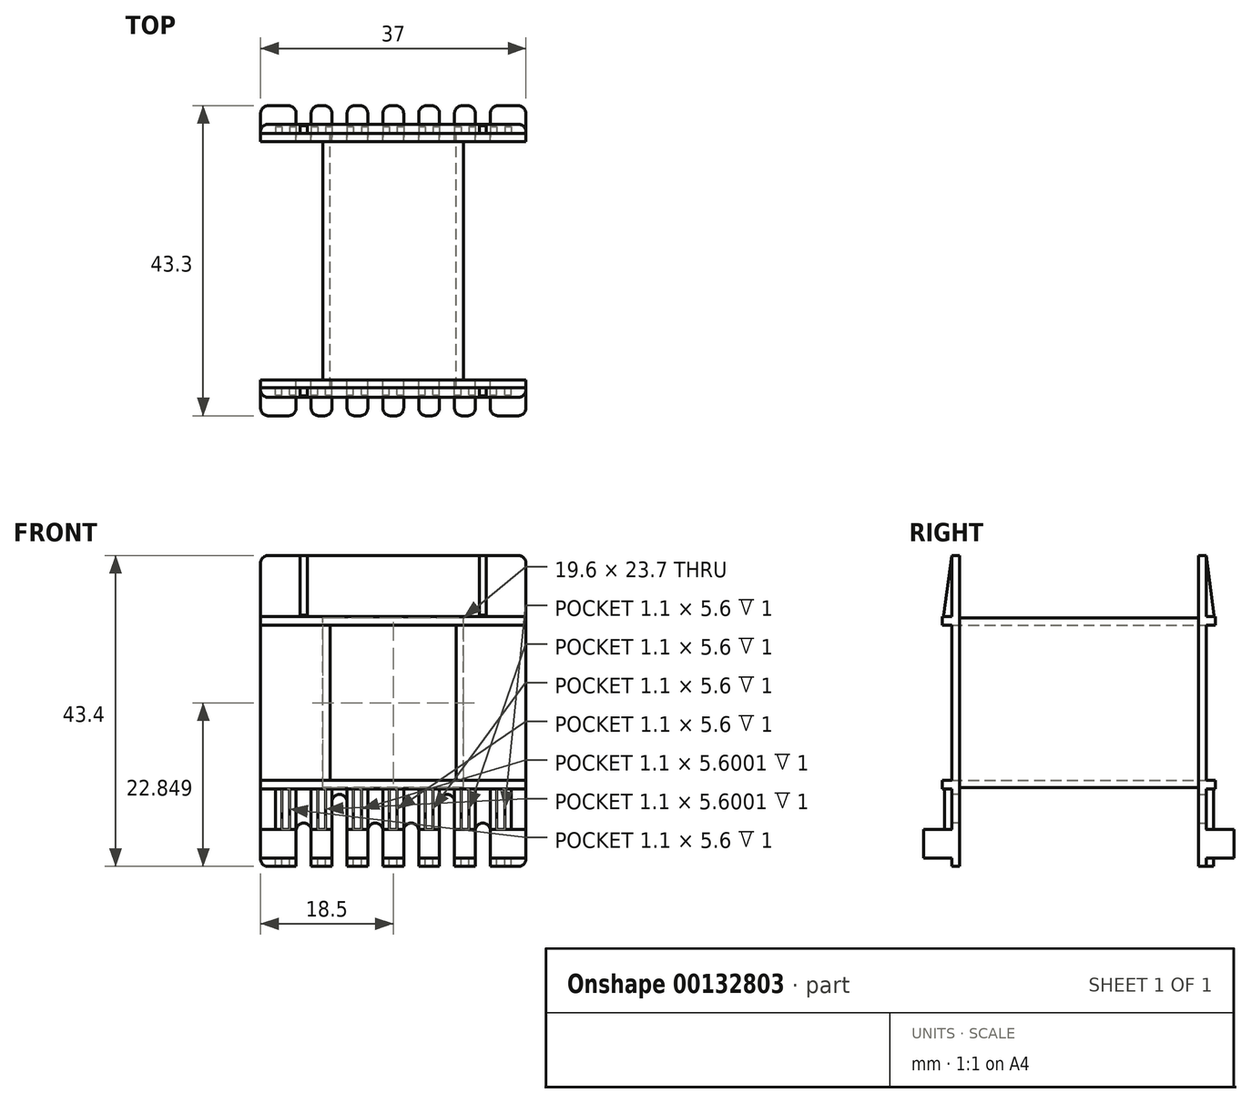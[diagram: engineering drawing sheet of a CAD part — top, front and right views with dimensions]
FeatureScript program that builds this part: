
annotation { "Feature Type Name" : "Feature", "Feature Type Description" : "" }
export const myFeature = defineFeature(function(context is Context, id is Id, definition is map)
    precondition{}
    {
        {
            var Q0;
            Q0=qCreatedBy(makeId("Front.planeOp"),FACE);
            var sketch = newSketch(context, id + "F0", { "sketchPlane" : qUnion([Q0])});
            skLineSegment(sketch, "E0.bottom", {"start": v(-18.5, -0.08) * mm, "end": v(18.5, -0.08) * mm});
            skLineSegment(sketch, "E0.top", {"start": v(-18.5, 43.32) * mm, "end": v(18.5, 43.32) * mm});
            skLineSegment(sketch, "E0.left", {"start": v(-18.5, -0.08) * mm, "end": v(-18.5, 43.32) * mm});
            skLineSegment(sketch, "E0.right", {"start": v(18.5, -0.08) * mm, "end": v(18.5, 43.32) * mm});
            skSolve(sketch);
        }
        {
            var Q0;
            Q0=makeQuery(id+"F0.imprint","IMPRINT",FACE,{"disambiguationData":[TD([[makeQuery(id+"F0.imprint","IMPRINT",EDGE,{"derivedFrom":sQuery(id+"F0.wireOp",EDGE,"E0.bottom")}),1.0]])]});
            var sketch = newSketch(context, id + "F1", { "sketchPlane" : qUnion([Q0])});
            skLineSegment(sketch, "E1.bottom", {"start": v(-8.8, 11.92) * mm, "end": v(8.8, 11.92) * mm});
            skLineSegment(sketch, "E1.top", {"start": v(-8.8, 33.62) * mm, "end": v(8.8, 33.62) * mm});
            skLineSegment(sketch, "E1.left", {"start": v(-8.8, 11.92) * mm, "end": v(-8.8, 33.62) * mm});
            skLineSegment(sketch, "E1.right", {"start": v(8.8, 11.92) * mm, "end": v(8.8, 33.62) * mm});
            skSolve(sketch);
        }
        {
            var Q0;
            Q0=makeQuery(id+"F1.imprint","IMPRINT",FACE,{"disambiguationData":[TD([[makeQuery(id+"F1.imprint","IMPRINT",EDGE,{"derivedFrom":sQuery(id+"F1.wireOp",EDGE,"E1.bottom")}),-1.0]])]});
            extrude(context, id + "F2", {"entities" : qUnion([Q0]), "depth" : 17.75 * mm, "hasSecondDirection" : true, "secondDirectionOppositeDirection" : false, "secondDirectionDepth" : 16.65 * mm});
        }
        {
            var Q0;
            Q0=makeQuery(id+"F2.opExtrude","CAP_FACE",FACE,{"disambiguationData":[OSD([sQuery(id+"F0.wireOp",EDGE,"E0.bottom"),sQuery(id+"F0.wireOp",EDGE,"E0.top"),sQuery(id+"F0.wireOp",EDGE,"E0.left"),sQuery(id+"F0.wireOp",EDGE,"E0.right"),sQuery(id+"F1.wireOp",EDGE,"E1.bottom"),sQuery(id+"F1.wireOp",EDGE,"E1.top"),sQuery(id+"F1.wireOp",EDGE,"E1.left"),sQuery(id+"F1.wireOp",EDGE,"E1.right")])],"isStart":false});
            var sketch = newSketch(context, id + "F3", { "sketchPlane" : qUnion([Q0])});
            skLineSegment(sketch, "E2.bottom", {"start": v(-18.5, 33.62) * mm, "end": v(18.5, 33.62) * mm});
            skLineSegment(sketch, "E2.top", {"start": v(-18.5, 34.82) * mm, "end": v(18.5, 34.82) * mm});
            skLineSegment(sketch, "E2.left", {"start": v(-18.5, 33.62) * mm, "end": v(-18.5, 34.82) * mm});
            skLineSegment(sketch, "E2.right", {"start": v(18.5, 33.62) * mm, "end": v(18.5, 34.82) * mm});
            skSolve(sketch);
        }
        {
            var Q0;
            Q0=qSketchRegion(id+"F3",true);
            extrude(context, id + "F4", {"entities" : qUnion([Q0]), "operationType" : NewBodyOperationType.ADD, "depth" : 1.3 * mm});
        }
        {
            var Q0;
            {var subQ0=sQuery(id+"F1.wireOp",EDGE,"E1.left");var subQ1=sQuery(id+"F1.wireOp",EDGE,"E1.top");var subQ2=sQuery(id+"F0.wireOp",EDGE,"E0.right");var subQ3=sQuery(id+"F1.wireOp",EDGE,"E1.right");var subQ4=sQuery(id+"F1.wireOp",EDGE,"E1.bottom");var subQ5=sQuery(id+"F0.wireOp",EDGE,"E0.bottom");var subQ6=sQuery(id+"F0.wireOp",EDGE,"E0.left");Q0=makeQuery(id+"F4.boolean.opBoolean","SPLIT",FACE,{"disambiguationData":[TD([makeQuery(id+"F2.opExtrude","SWEPT_FACE",FACE,{"disambiguationData":[OSD([subQ4])]})])],"derivedFrom":makeQuery(id+"F2.opExtrude","CAP_FACE",FACE,{"disambiguationData":[OSD([subQ5,sQuery(id+"F0.wireOp",EDGE,"E0.top"),subQ6,subQ2,subQ4,subQ1,subQ0,subQ3])],"isStart":false})});}
            var sketch = newSketch(context, id + "F5", { "sketchPlane" : qUnion([Q0])});
            skLineSegment(sketch, "E3.bottom", {"start": v(-18.5, 10.72) * mm, "end": v(18.5, 10.72) * mm});
            skLineSegment(sketch, "E3.top", {"start": v(-18.5, 11.92) * mm, "end": v(18.5, 11.92) * mm});
            skLineSegment(sketch, "E3.left", {"start": v(-18.5, 10.72) * mm, "end": v(-18.5, 11.92) * mm});
            skLineSegment(sketch, "E3.right", {"start": v(18.5, 10.72) * mm, "end": v(18.5, 11.92) * mm});
            skSolve(sketch);
        }
        {
            var Q0;
            Q0=makeQuery(id+"F5.imprint","IMPRINT",FACE,{"disambiguationData":[TD([[makeQuery(id+"F5.imprint","IMPRINT",EDGE,{"derivedFrom":sQuery(id+"F5.wireOp",EDGE,"E3.bottom")}),1.0]])]});
            extrude(context, id + "F6", {"entities" : qUnion([Q0]), "operationType" : NewBodyOperationType.ADD, "depth" : 1.3 * mm});
        }
        {
            var Q0;
            {var subQ0=sQuery(id+"F0.wireOp",EDGE,"E0.right");var subQ1=sQuery(id+"F0.wireOp",EDGE,"E0.left");var subQ2=sQuery(id+"F0.wireOp",EDGE,"E0.top");Q0=makeQuery(id+"F4.boolean.opBoolean","SPLIT",FACE,{"disambiguationData":[TD([makeQuery(id+"F2.opExtrude","SWEPT_FACE",FACE,{"disambiguationData":[OSD([subQ2])]})])],"derivedFrom":makeQuery(id+"F2.opExtrude","CAP_FACE",FACE,{"disambiguationData":[OSD([sQuery(id+"F0.wireOp",EDGE,"E0.bottom"),subQ2,subQ1,subQ0,sQuery(id+"F1.wireOp",EDGE,"E1.bottom"),sQuery(id+"F1.wireOp",EDGE,"E1.top"),sQuery(id+"F1.wireOp",EDGE,"E1.left"),sQuery(id+"F1.wireOp",EDGE,"E1.right")])],"isStart":false})});}
            var sketch = newSketch(context, id + "F7", { "sketchPlane" : qUnion([Q0])});
            skLineSegment(sketch, "E4.bottom", {"start": v(-13, 34.82) * mm, "end": v(-12, 34.82) * mm});
            skLineSegment(sketch, "E4.top", {"start": v(-13, 43.32) * mm, "end": v(-12, 43.32) * mm});
            skLineSegment(sketch, "E4.left", {"start": v(-13, 34.82) * mm, "end": v(-13, 43.32) * mm});
            skLineSegment(sketch, "E4.right", {"start": v(-12, 34.82) * mm, "end": v(-12, 43.32) * mm});
            skSolve(sketch);
        }
        {
            var Q0;
            {var subQ1=sQuery(id+"F0.wireOp",EDGE,"E0.top");var subQ2=makeQuery(id+"F2.opExtrude","SWEPT_FACE",FACE,{"disambiguationData":[OSD([subQ1])]});var subQ4=sQuery(id+"F0.wireOp",EDGE,"E0.right");var subQ5=makeQuery(id+"F2.opExtrude","SWEPT_FACE",FACE,{"disambiguationData":[OSD([subQ4])]});var subQ6=sQuery(id+"F0.wireOp",EDGE,"E0.left");Q0=makeQuery(id+"Fz3WZ2JE0xqVuv4_1.boolean.opBoolean","SPLIT",FACE,{"disambiguationData":[TD([subQ5])],"derivedFrom":makeQuery(id+"F4.boolean.opBoolean","SPLIT",FACE,{"disambiguationData":[TD([subQ2])],"derivedFrom":makeQuery(id+"F2.opExtrude","CAP_FACE",FACE,{"disambiguationData":[OSD([sQuery(id+"F0.wireOp",EDGE,"E0.bottom"),subQ1,subQ6,subQ4,sQuery(id+"F1.wireOp",EDGE,"E1.bottom"),sQuery(id+"F1.wireOp",EDGE,"E1.top"),sQuery(id+"F1.wireOp",EDGE,"E1.left"),sQuery(id+"F1.wireOp",EDGE,"E1.right")])],"isStart":false})})});}
            var sketch = newSketch(context, id + "F8", { "sketchPlane" : qUnion([Q0])});
            skLineSegment(sketch, "E5.bottom", {"start": v(12, 34.82) * mm, "end": v(13, 34.82) * mm});
            skLineSegment(sketch, "E5.top", {"start": v(12, 43.32) * mm, "end": v(13, 43.32) * mm});
            skLineSegment(sketch, "E5.left", {"start": v(12, 34.82) * mm, "end": v(12, 43.32) * mm});
            skLineSegment(sketch, "E5.right", {"start": v(13, 34.82) * mm, "end": v(13, 43.32) * mm});
            skSolve(sketch);
        }
        {
            var Q0;
            Q0=makeQuery(id+"F7.imprint","IMPRINT",FACE,{"disambiguationData":[TD([[makeQuery(id+"F7.imprint","IMPRINT",EDGE,{"derivedFrom":sQuery(id+"F7.wireOp",EDGE,"E4.bottom")}),1.0]])]});
            extrude(context, id + "F9", {"entities" : qUnion([Q0]), "operationType" : NewBodyOperationType.ADD, "depth" : 1.1 * mm});
        }
        {
            var Q0;
            Q0=makeQuery(id+"F8.imprint","IMPRINT",FACE,{"disambiguationData":[TD([[makeQuery(id+"F8.imprint","IMPRINT",EDGE,{"derivedFrom":sQuery(id+"F8.wireOp",EDGE,"E5.bottom")}),1.0]])]});
            extrude(context, id + "F10", {"entities" : qUnion([Q0]), "operationType" : NewBodyOperationType.ADD, "depth" : 1.1 * mm});
        }
        {
            var Q0;
            Q0=makeQuery(id+"F9.opExtrude","CAP_EDGE",EDGE,{"disambiguationData":[OSD([sQuery(id+"F7.wireOp",EDGE,"E4.top")])],"isStart":false});
            var Q1;
            Q1=makeQuery(id+"F10.opExtrude","CAP_EDGE",EDGE,{"disambiguationData":[OSD([sQuery(id+"F8.wireOp",EDGE,"E5.top")])],"isStart":false});
            chamfer(context, id + "F11", {"entities" : qUnion([Q0, Q1]), "chamferType" : ChamferType.TWO_OFFSETS, "width1" : 1.1 * mm, "oppositeDirection" : false, "width2" : 8.3 * mm, "tangentPropagation" : true});
        }
        {
            var Q0;
            {var subQ1=sQuery(id+"F0.wireOp",EDGE,"E0.right");var subQ3=sQuery(id+"F0.wireOp",EDGE,"E0.left");var subQ5=sQuery(id+"F0.wireOp",EDGE,"E0.bottom");var subQ6=makeQuery(id+"F2.opExtrude","SWEPT_FACE",FACE,{"disambiguationData":[OSD([subQ5])]});var subQ8=sQuery(id+"F1.wireOp",EDGE,"E1.left");var subQ9=sQuery(id+"F1.wireOp",EDGE,"E1.top");var subQ10=sQuery(id+"F1.wireOp",EDGE,"E1.right");var subQ11=sQuery(id+"F1.wireOp",EDGE,"E1.bottom");Q0=makeQuery(id+"F6.boolean.opBoolean","SPLIT",FACE,{"disambiguationData":[TD([subQ6])],"derivedFrom":makeQuery(id+"F4.boolean.opBoolean","SPLIT",FACE,{"disambiguationData":[TD([makeQuery(id+"F2.opExtrude","SWEPT_FACE",FACE,{"disambiguationData":[OSD([subQ11])]})])],"derivedFrom":makeQuery(id+"F2.opExtrude","CAP_FACE",FACE,{"disambiguationData":[OSD([subQ5,sQuery(id+"F0.wireOp",EDGE,"E0.top"),subQ3,subQ1,subQ11,subQ9,subQ8,subQ10])],"isStart":false})})});}
            var sketch = newSketch(context, id + "F12", { "sketchPlane" : qUnion([Q0])});
            skLineSegment(sketch, "E6.bottom", {"start": v(-16.45, -0.08) * mm, "end": v(-15.55, -0.08) * mm});
            skLineSegment(sketch, "E6.top", {"start": v(-16.45, 10.72) * mm, "end": v(-15.55, 10.72) * mm});
            skLineSegment(sketch, "E6.left", {"start": v(-16.45, -0.08) * mm, "end": v(-16.45, 10.72) * mm});
            skLineSegment(sketch, "E6.right", {"start": v(-15.55, -0.08) * mm, "end": v(-15.55, 10.72) * mm});
            skLineSegment(sketch, "E7.bottom", {"start": v(-14.45, -0.08) * mm, "end": v(-13.55, -0.08) * mm});
            skLineSegment(sketch, "E7.top", {"start": v(-14.45, 10.72) * mm, "end": v(-13.55, 10.72) * mm});
            skLineSegment(sketch, "E7.left", {"start": v(-14.45, -0.08) * mm, "end": v(-14.45, 10.72) * mm});
            skLineSegment(sketch, "E7.right", {"start": v(-13.55, -0.08) * mm, "end": v(-13.55, 10.72) * mm});
            skLineSegment(sketch, "E8.bottom", {"start": v(-11.45, -0.08) * mm, "end": v(-10.55, -0.08) * mm});
            skLineSegment(sketch, "E8.top", {"start": v(-11.45, 10.72) * mm, "end": v(-10.55, 10.72) * mm});
            skLineSegment(sketch, "E8.left", {"start": v(-11.45, -0.08) * mm, "end": v(-11.45, 10.72) * mm});
            skLineSegment(sketch, "E8.right", {"start": v(-10.55, -0.08) * mm, "end": v(-10.55, 10.72) * mm});
            skLineSegment(sketch, "E9.bottom", {"start": v(-9.45, -0.08) * mm, "end": v(-8.55, -0.08) * mm});
            skLineSegment(sketch, "E9.top", {"start": v(-9.45, 10.72) * mm, "end": v(-8.55, 10.72) * mm});
            skLineSegment(sketch, "E9.left", {"start": v(-9.45, -0.08) * mm, "end": v(-9.45, 10.72) * mm});
            skLineSegment(sketch, "E9.right", {"start": v(-8.55, -0.08) * mm, "end": v(-8.55, 10.72) * mm});
            skLineSegment(sketch, "E10.bottom", {"start": v(-6.45, -0.08) * mm, "end": v(-5.55, -0.08) * mm});
            skLineSegment(sketch, "E10.top", {"start": v(-6.45, 10.72) * mm, "end": v(-5.55, 10.72) * mm});
            skLineSegment(sketch, "E10.left", {"start": v(-6.45, -0.08) * mm, "end": v(-6.45, 10.72) * mm});
            skLineSegment(sketch, "E10.right", {"start": v(-5.55, -0.08) * mm, "end": v(-5.55, 10.72) * mm});
            skLineSegment(sketch, "E11.bottom", {"start": v(-1.45, -0.08) * mm, "end": v(-0.55, -0.08) * mm});
            skLineSegment(sketch, "E11.top", {"start": v(-1.45, 10.72) * mm, "end": v(-0.55, 10.72) * mm});
            skLineSegment(sketch, "E11.left", {"start": v(-1.45, -0.08) * mm, "end": v(-1.45, 10.72) * mm});
            skLineSegment(sketch, "E11.right", {"start": v(-0.55, -0.08) * mm, "end": v(-0.55, 10.72) * mm});
            skLineSegment(sketch, "E12.bottom", {"start": v(0.55, -0.08) * mm, "end": v(1.45, -0.08) * mm});
            skLineSegment(sketch, "E12.top", {"start": v(0.55, 10.72) * mm, "end": v(1.45, 10.72) * mm});
            skLineSegment(sketch, "E12.left", {"start": v(0.55, -0.08) * mm, "end": v(0.55, 10.72) * mm});
            skLineSegment(sketch, "E12.right", {"start": v(1.45, -0.08) * mm, "end": v(1.45, 10.72) * mm});
            skLineSegment(sketch, "E13.bottom", {"start": v(3.55, -0.08) * mm, "end": v(4.45, -0.08) * mm});
            skLineSegment(sketch, "E13.top", {"start": v(3.55, 10.72) * mm, "end": v(4.45, 10.72) * mm});
            skLineSegment(sketch, "E13.left", {"start": v(3.55, -0.08) * mm, "end": v(3.55, 10.72) * mm});
            skLineSegment(sketch, "E13.right", {"start": v(4.45, -0.08) * mm, "end": v(4.45, 10.72) * mm});
            skLineSegment(sketch, "E14.bottom", {"start": v(5.55, -0.08) * mm, "end": v(6.45, -0.08) * mm});
            skLineSegment(sketch, "E14.top", {"start": v(5.55, 10.72) * mm, "end": v(6.45, 10.72) * mm});
            skLineSegment(sketch, "E14.left", {"start": v(5.55, -0.08) * mm, "end": v(5.55, 10.72) * mm});
            skLineSegment(sketch, "E14.right", {"start": v(6.45, -0.08) * mm, "end": v(6.45, 10.72) * mm});
            skLineSegment(sketch, "E15.bottom", {"start": v(8.55, -0.08) * mm, "end": v(9.45, -0.08) * mm});
            skLineSegment(sketch, "E15.top", {"start": v(8.55, 10.72) * mm, "end": v(9.45, 10.72) * mm});
            skLineSegment(sketch, "E15.left", {"start": v(8.55, -0.08) * mm, "end": v(8.55, 10.72) * mm});
            skLineSegment(sketch, "E15.right", {"start": v(9.45, -0.08) * mm, "end": v(9.45, 10.72) * mm});
            skLineSegment(sketch, "E16.bottom", {"start": v(10.55, -0.08) * mm, "end": v(11.45, -0.08) * mm});
            skLineSegment(sketch, "E16.top", {"start": v(10.55, 10.72) * mm, "end": v(11.45, 10.72) * mm});
            skLineSegment(sketch, "E16.left", {"start": v(10.55, -0.08) * mm, "end": v(10.55, 10.72) * mm});
            skLineSegment(sketch, "E16.right", {"start": v(11.45, -0.08) * mm, "end": v(11.45, 10.72) * mm});
            skLineSegment(sketch, "E17.bottom", {"start": v(13.55, -0.08) * mm, "end": v(14.45, -0.08) * mm});
            skLineSegment(sketch, "E17.top", {"start": v(13.55, 10.72) * mm, "end": v(14.45, 10.72) * mm});
            skLineSegment(sketch, "E17.left", {"start": v(13.55, -0.08) * mm, "end": v(13.55, 10.72) * mm});
            skLineSegment(sketch, "E17.right", {"start": v(14.45, -0.08) * mm, "end": v(14.45, 10.72) * mm});
            skLineSegment(sketch, "E18.bottom", {"start": v(15.55, -0.08) * mm, "end": v(16.45, -0.08) * mm});
            skLineSegment(sketch, "E18.top", {"start": v(15.55, 10.72) * mm, "end": v(16.45, 10.72) * mm});
            skLineSegment(sketch, "E18.left", {"start": v(15.55, -0.08) * mm, "end": v(15.55, 10.72) * mm});
            skLineSegment(sketch, "E18.right", {"start": v(16.45, -0.08) * mm, "end": v(16.45, 10.72) * mm});
            skLineSegment(sketch, "E19.bottom", {"start": v(-4.45, -0.08) * mm, "end": v(-3.55, -0.08) * mm});
            skLineSegment(sketch, "E19.top", {"start": v(-4.45, 10.72) * mm, "end": v(-3.55, 10.72) * mm});
            skLineSegment(sketch, "E19.left", {"start": v(-4.45, -0.08) * mm, "end": v(-4.45, 10.72) * mm});
            skLineSegment(sketch, "E19.right", {"start": v(-3.55, -0.08) * mm, "end": v(-3.55, 10.72) * mm});
            skSolve(sketch);
        }
        {
            var Q0;
            Q0=makeQuery(id+"F12.imprint","IMPRINT",FACE,{"disambiguationData":[TD([[makeQuery(id+"F12.imprint","IMPRINT",EDGE,{"derivedFrom":sQuery(id+"F12.wireOp",EDGE,"E6.bottom")}),1.0]])]});
            var Q1;
            Q1=makeQuery(id+"F12.imprint","IMPRINT",FACE,{"disambiguationData":[TD([[makeQuery(id+"F12.imprint","IMPRINT",EDGE,{"derivedFrom":sQuery(id+"F12.wireOp",EDGE,"E7.bottom")}),1.0]])]});
            var Q2;
            Q2=makeQuery(id+"F12.imprint","IMPRINT",FACE,{"disambiguationData":[TD([[makeQuery(id+"F12.imprint","IMPRINT",EDGE,{"derivedFrom":sQuery(id+"F12.wireOp",EDGE,"E8.bottom")}),1.0]])]});
            var Q3;
            Q3=makeQuery(id+"F12.imprint","IMPRINT",FACE,{"disambiguationData":[TD([[makeQuery(id+"F12.imprint","IMPRINT",EDGE,{"derivedFrom":sQuery(id+"F12.wireOp",EDGE,"E9.bottom")}),1.0]])]});
            var Q4;
            Q4=makeQuery(id+"F12.imprint","IMPRINT",FACE,{"disambiguationData":[TD([[makeQuery(id+"F12.imprint","IMPRINT",EDGE,{"derivedFrom":sQuery(id+"F12.wireOp",EDGE,"E10.bottom")}),1.0]])]});
            var Q5;
            Q5=makeQuery(id+"F12.imprint","IMPRINT",FACE,{"disambiguationData":[TD([[makeQuery(id+"F12.imprint","IMPRINT",EDGE,{"derivedFrom":sQuery(id+"F12.wireOp",EDGE,"E19.bottom")}),1.0]])]});
            var Q6;
            Q6=makeQuery(id+"F12.imprint","IMPRINT",FACE,{"disambiguationData":[TD([[makeQuery(id+"F12.imprint","IMPRINT",EDGE,{"derivedFrom":sQuery(id+"F12.wireOp",EDGE,"E11.bottom")}),1.0]])]});
            var Q7;
            Q7=makeQuery(id+"F12.imprint","IMPRINT",FACE,{"disambiguationData":[TD([[makeQuery(id+"F12.imprint","IMPRINT",EDGE,{"derivedFrom":sQuery(id+"F12.wireOp",EDGE,"E12.bottom")}),1.0]])]});
            var Q8;
            Q8=makeQuery(id+"F12.imprint","IMPRINT",FACE,{"disambiguationData":[TD([[makeQuery(id+"F12.imprint","IMPRINT",EDGE,{"derivedFrom":sQuery(id+"F12.wireOp",EDGE,"E13.bottom")}),1.0]])]});
            var Q9;
            Q9=makeQuery(id+"F12.imprint","IMPRINT",FACE,{"disambiguationData":[TD([[makeQuery(id+"F12.imprint","IMPRINT",EDGE,{"derivedFrom":sQuery(id+"F12.wireOp",EDGE,"E14.bottom")}),1.0]])]});
            var Q10;
            Q10=makeQuery(id+"F12.imprint","IMPRINT",FACE,{"disambiguationData":[TD([[makeQuery(id+"F12.imprint","IMPRINT",EDGE,{"derivedFrom":sQuery(id+"F12.wireOp",EDGE,"E15.bottom")}),1.0]])]});
            var Q11;
            Q11=makeQuery(id+"F12.imprint","IMPRINT",FACE,{"disambiguationData":[TD([[makeQuery(id+"F12.imprint","IMPRINT",EDGE,{"derivedFrom":sQuery(id+"F12.wireOp",EDGE,"E16.bottom")}),1.0]])]});
            var Q12;
            Q12=makeQuery(id+"F12.imprint","IMPRINT",FACE,{"disambiguationData":[TD([[makeQuery(id+"F12.imprint","IMPRINT",EDGE,{"derivedFrom":sQuery(id+"F12.wireOp",EDGE,"E17.bottom")}),1.0]])]});
            var Q13;
            Q13=makeQuery(id+"F12.imprint","IMPRINT",FACE,{"disambiguationData":[TD([[makeQuery(id+"F12.imprint","IMPRINT",EDGE,{"derivedFrom":sQuery(id+"F12.wireOp",EDGE,"E18.bottom")}),1.0]])]});
            extrude(context, id + "F13", {"entities" : qUnion([Q0, Q1, Q2, Q3, Q4, Q5, Q6, Q7, Q8, Q9, Q10, Q11, Q12, Q13]), "operationType" : NewBodyOperationType.ADD, "depth" : 1 * mm});
        }
        {
            var Q0;
            {var subQ2=sQuery(id+"F0.wireOp",EDGE,"E0.bottom");var subQ3=makeQuery(id+"F2.opExtrude","SWEPT_FACE",FACE,{"disambiguationData":[OSD([subQ2])]});var subQ4=sQuery(id+"F0.wireOp",EDGE,"E0.left");var subQ5=makeQuery(id+"F2.opExtrude","SWEPT_FACE",FACE,{"disambiguationData":[OSD([subQ4])]});var subQ7=sQuery(id+"F0.wireOp",EDGE,"E0.right");var subQ10=sQuery(id+"F1.wireOp",EDGE,"E1.left");var subQ11=sQuery(id+"F1.wireOp",EDGE,"E1.top");var subQ12=sQuery(id+"F1.wireOp",EDGE,"E1.right");var subQ13=sQuery(id+"F1.wireOp",EDGE,"E1.bottom");Q0=makeQuery(id+"F13.boolean.opBoolean","SPLIT",FACE,{"disambiguationData":[TD([subQ5])],"derivedFrom":makeQuery(id+"F6.boolean.opBoolean","SPLIT",FACE,{"disambiguationData":[TD([subQ3])],"derivedFrom":makeQuery(id+"F4.boolean.opBoolean","SPLIT",FACE,{"disambiguationData":[TD([makeQuery(id+"F2.opExtrude","SWEPT_FACE",FACE,{"disambiguationData":[OSD([subQ13])]})])],"derivedFrom":makeQuery(id+"F2.opExtrude","CAP_FACE",FACE,{"disambiguationData":[OSD([subQ2,sQuery(id+"F0.wireOp",EDGE,"E0.top"),subQ4,subQ7,subQ13,subQ11,subQ10,subQ12])],"isStart":false})})})});}
            var sketch = newSketch(context, id + "F14", { "sketchPlane" : qUnion([Q0])});
            skLineSegment(sketch, "E20.bottom", {"start": v(-18.5, 1.12) * mm, "end": v(-13.55, 1.12) * mm});
            skLineSegment(sketch, "E20.top", {"start": v(-18.5, 5.12) * mm, "end": v(-13.55, 5.12) * mm});
            skLineSegment(sketch, "E20.left", {"start": v(-18.5, 1.12) * mm, "end": v(-18.5, 5.12) * mm});
            skLineSegment(sketch, "E20.right", {"start": v(-13.55, 1.12) * mm, "end": v(-13.55, 5.12) * mm});
            skLineSegment(sketch, "E21.bottom", {"start": v(-11.45, 1.12) * mm, "end": v(-8.55, 1.12) * mm});
            skLineSegment(sketch, "E21.top", {"start": v(-11.45, 5.12) * mm, "end": v(-8.55, 5.12) * mm});
            skLineSegment(sketch, "E21.left", {"start": v(-11.45, 1.12) * mm, "end": v(-11.45, 5.12) * mm});
            skLineSegment(sketch, "E21.right", {"start": v(-8.55, 1.12) * mm, "end": v(-8.55, 5.12) * mm});
            skPoint(sketch, "E22.firstSnap0", {"position": v(-16.02, 1.12) * mm});
            skLineSegment(sketch, "E22.bottom", {"start": v(-6.45, 1.12) * mm, "end": v(-3.55, 1.12) * mm});
            skLineSegment(sketch, "E22.top", {"start": v(-6.45, 5.12) * mm, "end": v(-3.55, 5.12) * mm});
            skLineSegment(sketch, "E22.left", {"start": v(-6.45, 1.12) * mm, "end": v(-6.45, 5.12) * mm});
            skLineSegment(sketch, "E22.right", {"start": v(-3.55, 1.12) * mm, "end": v(-3.55, 5.12) * mm});
            skLineSegment(sketch, "E23.bottom", {"start": v(-1.45, 1.12) * mm, "end": v(1.45, 1.12) * mm});
            skLineSegment(sketch, "E23.top", {"start": v(-1.45, 5.12) * mm, "end": v(1.45, 5.12) * mm});
            skLineSegment(sketch, "E23.left", {"start": v(-1.45, 1.12) * mm, "end": v(-1.45, 5.12) * mm});
            skLineSegment(sketch, "E23.right", {"start": v(1.45, 1.12) * mm, "end": v(1.45, 5.12) * mm});
            skLineSegment(sketch, "E24.bottom", {"start": v(3.55, 1.12) * mm, "end": v(6.45, 1.12) * mm});
            skLineSegment(sketch, "E24.top", {"start": v(3.55, 5.12) * mm, "end": v(6.45, 5.12) * mm});
            skLineSegment(sketch, "E24.left", {"start": v(3.55, 1.12) * mm, "end": v(3.55, 5.12) * mm});
            skLineSegment(sketch, "E24.right", {"start": v(6.45, 1.12) * mm, "end": v(6.45, 5.12) * mm});
            skLineSegment(sketch, "E25.bottom", {"start": v(8.55, 1.12) * mm, "end": v(11.45, 1.12) * mm});
            skLineSegment(sketch, "E25.top", {"start": v(8.55, 5.12) * mm, "end": v(11.45, 5.12) * mm});
            skLineSegment(sketch, "E25.left", {"start": v(8.55, 1.12) * mm, "end": v(8.55, 5.12) * mm});
            skLineSegment(sketch, "E25.right", {"start": v(11.45, 1.12) * mm, "end": v(11.45, 5.12) * mm});
            skLineSegment(sketch, "E26.bottom", {"start": v(13.55, 1.12) * mm, "end": v(18.5, 1.12) * mm});
            skLineSegment(sketch, "E26.top", {"start": v(13.55, 5.12) * mm, "end": v(18.5, 5.12) * mm});
            skLineSegment(sketch, "E26.left", {"start": v(13.55, 1.12) * mm, "end": v(13.55, 5.12) * mm});
            skLineSegment(sketch, "E26.right", {"start": v(18.5, 1.12) * mm, "end": v(18.5, 5.12) * mm});
            skSolve(sketch);
        }
        {
            var Q0;
            {var subQ0=sQuery(id+"F14.wireOp",EDGE,"E20.left");Q0=makeQuery(id+"F14.imprint","IMPRINT",FACE,{"disambiguationData":[TD([[makeQuery(id+"F14.imprint","IMPRINT",EDGE,{"derivedFrom":subQ0}),-1.0]])]});}
            var Q1;
            {var subQ0=sQuery(id+"F14.wireOp",EDGE,"E20.right");Q1=makeQuery(id+"F14.imprint","IMPRINT",FACE,{"disambiguationData":[TD([[makeQuery(id+"F14.imprint","IMPRINT",EDGE,{"derivedFrom":subQ0}),1.0]])]});}
            var Q2;
            Q2=makeQuery(id+"F14.imprint","IMPRINT",FACE,{"disambiguationData":[TD([[makeQuery(id+"F14.imprint","IMPRINT",EDGE,{"derivedFrom":sQuery(id+"F14.wireOp",EDGE,"E21.bottom")}),1.0]])]});
            var Q3;
            Q3=makeQuery(id+"F14.imprint","IMPRINT",FACE,{"disambiguationData":[TD([[makeQuery(id+"F14.imprint","IMPRINT",EDGE,{"derivedFrom":sQuery(id+"F14.wireOp",EDGE,"E22.bottom")}),1.0]])]});
            var Q4;
            Q4=makeQuery(id+"F14.imprint","IMPRINT",FACE,{"disambiguationData":[TD([[makeQuery(id+"F14.imprint","IMPRINT",EDGE,{"derivedFrom":sQuery(id+"F14.wireOp",EDGE,"E23.bottom")}),1.0]])]});
            var Q5;
            Q5=makeQuery(id+"F14.imprint","IMPRINT",FACE,{"disambiguationData":[TD([[makeQuery(id+"F14.imprint","IMPRINT",EDGE,{"derivedFrom":sQuery(id+"F14.wireOp",EDGE,"E24.bottom")}),1.0]])]});
            var Q6;
            Q6=makeQuery(id+"F14.imprint","IMPRINT",FACE,{"disambiguationData":[TD([[makeQuery(id+"F14.imprint","IMPRINT",EDGE,{"derivedFrom":sQuery(id+"F14.wireOp",EDGE,"E25.bottom")}),1.0]])]});
            var Q7;
            Q7=makeQuery(id+"F14.imprint","IMPRINT",FACE,{"disambiguationData":[TD([[makeQuery(id+"F14.imprint","IMPRINT",EDGE,{"derivedFrom":sQuery(id+"F14.wireOp",EDGE,"E26.bottom")}),1.0]])]});
            extrude(context, id + "F15", {"entities" : qUnion([Q0, Q1, Q2, Q3, Q4, Q5, Q6, Q7]), "operationType" : NewBodyOperationType.ADD, "depth" : 3.9 * mm});
        }
        {
            var Q0;
            {var subQ0=sQuery(id+"F0.wireOp",EDGE,"E0.bottom");var subQ1=makeQuery(id+"F2.opExtrude","SWEPT_FACE",FACE,{"disambiguationData":[OSD([subQ0])]});var subQ4=sQuery(id+"F0.wireOp",EDGE,"E0.right");var subQ6=sQuery(id+"F0.wireOp",EDGE,"E0.left");var subQ9=sQuery(id+"F1.wireOp",EDGE,"E1.left");var subQ10=sQuery(id+"F1.wireOp",EDGE,"E1.top");var subQ11=sQuery(id+"F1.wireOp",EDGE,"E1.right");var subQ12=sQuery(id+"F1.wireOp",EDGE,"E1.bottom");Q0=makeQuery(id+"F13.boolean.opBoolean","SPLIT",FACE,{"disambiguationData":[TD([makeQuery(id+"F13.opExtrude","SWEPT_FACE",FACE,{"disambiguationData":[OSD([sQuery(id+"F12.wireOp",EDGE,"E7.right")])]})])],"derivedFrom":makeQuery(id+"F6.boolean.opBoolean","SPLIT",FACE,{"disambiguationData":[TD([subQ1])],"derivedFrom":makeQuery(id+"F4.boolean.opBoolean","SPLIT",FACE,{"disambiguationData":[TD([makeQuery(id+"F2.opExtrude","SWEPT_FACE",FACE,{"disambiguationData":[OSD([subQ12])]})])],"derivedFrom":makeQuery(id+"F2.opExtrude","CAP_FACE",FACE,{"disambiguationData":[OSD([subQ0,sQuery(id+"F0.wireOp",EDGE,"E0.top"),subQ6,subQ4,subQ12,subQ10,subQ9,subQ11])],"isStart":false})})})});}
            var sketch = newSketch(context, id + "F16", { "sketchPlane" : qUnion([Q0])});
            skLineSegment(sketch, "E27.bottom", {"start": v(-13.55, -0.08) * mm, "end": v(-11.45, -0.08) * mm});
            skLineSegment(sketch, "E27.top", {"start": v(-13.55, 4.92) * mm, "end": v(-11.45, 4.92) * mm});
            skLineSegment(sketch, "E27.left", {"start": v(-13.55, -0.08) * mm, "end": v(-13.55, 4.92) * mm});
            skLineSegment(sketch, "E27.right", {"start": v(-11.45, -0.08) * mm, "end": v(-11.45, 4.92) * mm});
            skArc(sketch, "E28", {"start": v(-11.45, 4.92) * mm, "mid": v(-12.5, 5.97) * mm, "end": v(-13.55, 4.92) * mm});
            skSolve(sketch);
        }
        {
            var Q0;
            {var subQ0=sQuery(id+"F0.wireOp",EDGE,"E0.bottom");var subQ1=makeQuery(id+"F2.opExtrude","SWEPT_FACE",FACE,{"disambiguationData":[OSD([subQ0])]});var subQ4=sQuery(id+"F0.wireOp",EDGE,"E0.right");var subQ6=sQuery(id+"F0.wireOp",EDGE,"E0.left");var subQ9=sQuery(id+"F1.wireOp",EDGE,"E1.left");var subQ10=sQuery(id+"F1.wireOp",EDGE,"E1.top");var subQ11=sQuery(id+"F1.wireOp",EDGE,"E1.right");var subQ12=sQuery(id+"F1.wireOp",EDGE,"E1.bottom");Q0=makeQuery(id+"F13.boolean.opBoolean","SPLIT",FACE,{"disambiguationData":[TD([makeQuery(id+"F13.opExtrude","SWEPT_FACE",FACE,{"disambiguationData":[OSD([sQuery(id+"F12.wireOp",EDGE,"E9.right")])]})])],"derivedFrom":makeQuery(id+"F6.boolean.opBoolean","SPLIT",FACE,{"disambiguationData":[TD([subQ1])],"derivedFrom":makeQuery(id+"F4.boolean.opBoolean","SPLIT",FACE,{"disambiguationData":[TD([makeQuery(id+"F2.opExtrude","SWEPT_FACE",FACE,{"disambiguationData":[OSD([subQ12])]})])],"derivedFrom":makeQuery(id+"F2.opExtrude","CAP_FACE",FACE,{"disambiguationData":[OSD([subQ0,sQuery(id+"F0.wireOp",EDGE,"E0.top"),subQ6,subQ4,subQ12,subQ10,subQ9,subQ11])],"isStart":false})})})});}
            var sketch = newSketch(context, id + "F17", { "sketchPlane" : qUnion([Q0])});
            skLineSegment(sketch, "E29.bottom", {"start": v(-8.55, -0.08) * mm, "end": v(-6.45, -0.08) * mm});
            skLineSegment(sketch, "E29.top", {"start": v(-8.55, 8.92) * mm, "end": v(-6.45, 8.92) * mm});
            skLineSegment(sketch, "E29.left", {"start": v(-8.55, -0.08) * mm, "end": v(-8.55, 8.92) * mm});
            skLineSegment(sketch, "E29.right", {"start": v(-6.45, -0.08) * mm, "end": v(-6.45, 8.92) * mm});
            skArc(sketch, "E30", {"start": v(-6.45, 8.92) * mm, "mid": v(-7.5, 9.97) * mm, "end": v(-8.55, 8.92) * mm});
            skSolve(sketch);
        }
        {
            var Q0;
            {var subQ0=sQuery(id+"F0.wireOp",EDGE,"E0.bottom");var subQ1=makeQuery(id+"F2.opExtrude","SWEPT_FACE",FACE,{"disambiguationData":[OSD([subQ0])]});var subQ4=sQuery(id+"F0.wireOp",EDGE,"E0.right");var subQ6=sQuery(id+"F0.wireOp",EDGE,"E0.left");var subQ9=sQuery(id+"F1.wireOp",EDGE,"E1.left");var subQ10=sQuery(id+"F1.wireOp",EDGE,"E1.top");var subQ11=sQuery(id+"F1.wireOp",EDGE,"E1.right");var subQ12=sQuery(id+"F1.wireOp",EDGE,"E1.bottom");Q0=makeQuery(id+"F13.boolean.opBoolean","SPLIT",FACE,{"disambiguationData":[TD([makeQuery(id+"F13.opExtrude","SWEPT_FACE",FACE,{"disambiguationData":[OSD([sQuery(id+"F12.wireOp",EDGE,"E11.left")])]})])],"derivedFrom":makeQuery(id+"F6.boolean.opBoolean","SPLIT",FACE,{"disambiguationData":[TD([subQ1])],"derivedFrom":makeQuery(id+"F4.boolean.opBoolean","SPLIT",FACE,{"disambiguationData":[TD([makeQuery(id+"F2.opExtrude","SWEPT_FACE",FACE,{"disambiguationData":[OSD([subQ12])]})])],"derivedFrom":makeQuery(id+"F2.opExtrude","CAP_FACE",FACE,{"disambiguationData":[OSD([subQ0,sQuery(id+"F0.wireOp",EDGE,"E0.top"),subQ6,subQ4,subQ12,subQ10,subQ9,subQ11])],"isStart":false})})})});}
            var sketch = newSketch(context, id + "F18", { "sketchPlane" : qUnion([Q0])});
            skLineSegment(sketch, "E31.bottom", {"start": v(-3.55, -0.08) * mm, "end": v(-1.45, -0.08) * mm});
            skLineSegment(sketch, "E31.top", {"start": v(-3.55, 4.92) * mm, "end": v(-1.45, 4.92) * mm});
            skLineSegment(sketch, "E31.left", {"start": v(-3.55, -0.08) * mm, "end": v(-3.55, 4.92) * mm});
            skLineSegment(sketch, "E31.right", {"start": v(-1.45, -0.08) * mm, "end": v(-1.45, 4.92) * mm});
            skArc(sketch, "E32", {"start": v(-1.45, 4.92) * mm, "mid": v(-2.5, 5.97) * mm, "end": v(-3.55, 4.92) * mm});
            skSolve(sketch);
        }
        {
            var Q0;
            {var subQ0=sQuery(id+"F0.wireOp",EDGE,"E0.bottom");var subQ1=makeQuery(id+"F2.opExtrude","SWEPT_FACE",FACE,{"disambiguationData":[OSD([subQ0])]});var subQ4=sQuery(id+"F0.wireOp",EDGE,"E0.right");var subQ6=sQuery(id+"F0.wireOp",EDGE,"E0.left");var subQ9=sQuery(id+"F1.wireOp",EDGE,"E1.left");var subQ10=sQuery(id+"F1.wireOp",EDGE,"E1.top");var subQ11=sQuery(id+"F1.wireOp",EDGE,"E1.right");var subQ12=sQuery(id+"F1.wireOp",EDGE,"E1.bottom");Q0=makeQuery(id+"F13.boolean.opBoolean","SPLIT",FACE,{"disambiguationData":[TD([makeQuery(id+"F13.opExtrude","SWEPT_FACE",FACE,{"disambiguationData":[OSD([sQuery(id+"F12.wireOp",EDGE,"E12.right")])]})])],"derivedFrom":makeQuery(id+"F6.boolean.opBoolean","SPLIT",FACE,{"disambiguationData":[TD([subQ1])],"derivedFrom":makeQuery(id+"F4.boolean.opBoolean","SPLIT",FACE,{"disambiguationData":[TD([makeQuery(id+"F2.opExtrude","SWEPT_FACE",FACE,{"disambiguationData":[OSD([subQ12])]})])],"derivedFrom":makeQuery(id+"F2.opExtrude","CAP_FACE",FACE,{"disambiguationData":[OSD([subQ0,sQuery(id+"F0.wireOp",EDGE,"E0.top"),subQ6,subQ4,subQ12,subQ10,subQ9,subQ11])],"isStart":false})})})});}
            var sketch = newSketch(context, id + "F19", { "sketchPlane" : qUnion([Q0])});
            skLineSegment(sketch, "E33.bottom", {"start": v(1.45, -0.08) * mm, "end": v(3.55, -0.08) * mm});
            skLineSegment(sketch, "E33.top", {"start": v(1.45, 4.92) * mm, "end": v(3.55, 4.92) * mm});
            skLineSegment(sketch, "E33.left", {"start": v(1.45, -0.08) * mm, "end": v(1.45, 4.92) * mm});
            skLineSegment(sketch, "E33.right", {"start": v(3.55, -0.08) * mm, "end": v(3.55, 4.92) * mm});
            skArc(sketch, "E34", {"start": v(3.55, 4.92) * mm, "mid": v(2.5, 5.97) * mm, "end": v(1.45, 4.92) * mm});
            skSolve(sketch);
        }
        {
            var Q0;
            {var subQ0=sQuery(id+"F0.wireOp",EDGE,"E0.bottom");var subQ1=makeQuery(id+"F2.opExtrude","SWEPT_FACE",FACE,{"disambiguationData":[OSD([subQ0])]});var subQ4=sQuery(id+"F0.wireOp",EDGE,"E0.right");var subQ6=sQuery(id+"F0.wireOp",EDGE,"E0.left");var subQ9=sQuery(id+"F1.wireOp",EDGE,"E1.left");var subQ10=sQuery(id+"F1.wireOp",EDGE,"E1.top");var subQ11=sQuery(id+"F1.wireOp",EDGE,"E1.right");var subQ12=sQuery(id+"F1.wireOp",EDGE,"E1.bottom");Q0=makeQuery(id+"F13.boolean.opBoolean","SPLIT",FACE,{"disambiguationData":[TD([makeQuery(id+"F13.opExtrude","SWEPT_FACE",FACE,{"disambiguationData":[OSD([sQuery(id+"F12.wireOp",EDGE,"E14.right")])]})])],"derivedFrom":makeQuery(id+"F6.boolean.opBoolean","SPLIT",FACE,{"disambiguationData":[TD([subQ1])],"derivedFrom":makeQuery(id+"F4.boolean.opBoolean","SPLIT",FACE,{"disambiguationData":[TD([makeQuery(id+"F2.opExtrude","SWEPT_FACE",FACE,{"disambiguationData":[OSD([subQ12])]})])],"derivedFrom":makeQuery(id+"F2.opExtrude","CAP_FACE",FACE,{"disambiguationData":[OSD([subQ0,sQuery(id+"F0.wireOp",EDGE,"E0.top"),subQ6,subQ4,subQ12,subQ10,subQ9,subQ11])],"isStart":false})})})});}
            var sketch = newSketch(context, id + "F20", { "sketchPlane" : qUnion([Q0])});
            skLineSegment(sketch, "E35.bottom", {"start": v(6.45, -0.08) * mm, "end": v(8.55, -0.08) * mm});
            skLineSegment(sketch, "E35.top", {"start": v(6.45, 8.92) * mm, "end": v(8.55, 8.92) * mm});
            skLineSegment(sketch, "E35.left", {"start": v(6.45, -0.08) * mm, "end": v(6.45, 8.92) * mm});
            skLineSegment(sketch, "E35.right", {"start": v(8.55, -0.08) * mm, "end": v(8.55, 8.92) * mm});
            skArc(sketch, "E36", {"start": v(8.55, 8.92) * mm, "mid": v(7.5, 9.97) * mm, "end": v(6.45, 8.92) * mm});
            skSolve(sketch);
        }
        {
            var Q0;
            {var subQ0=sQuery(id+"F0.wireOp",EDGE,"E0.bottom");var subQ1=makeQuery(id+"F2.opExtrude","SWEPT_FACE",FACE,{"disambiguationData":[OSD([subQ0])]});var subQ4=sQuery(id+"F0.wireOp",EDGE,"E0.right");var subQ6=sQuery(id+"F0.wireOp",EDGE,"E0.left");var subQ9=sQuery(id+"F1.wireOp",EDGE,"E1.left");var subQ10=sQuery(id+"F1.wireOp",EDGE,"E1.top");var subQ11=sQuery(id+"F1.wireOp",EDGE,"E1.right");var subQ12=sQuery(id+"F1.wireOp",EDGE,"E1.bottom");Q0=makeQuery(id+"F13.boolean.opBoolean","SPLIT",FACE,{"disambiguationData":[TD([makeQuery(id+"F13.opExtrude","SWEPT_FACE",FACE,{"disambiguationData":[OSD([sQuery(id+"F12.wireOp",EDGE,"E16.right")])]})])],"derivedFrom":makeQuery(id+"F6.boolean.opBoolean","SPLIT",FACE,{"disambiguationData":[TD([subQ1])],"derivedFrom":makeQuery(id+"F4.boolean.opBoolean","SPLIT",FACE,{"disambiguationData":[TD([makeQuery(id+"F2.opExtrude","SWEPT_FACE",FACE,{"disambiguationData":[OSD([subQ12])]})])],"derivedFrom":makeQuery(id+"F2.opExtrude","CAP_FACE",FACE,{"disambiguationData":[OSD([subQ0,sQuery(id+"F0.wireOp",EDGE,"E0.top"),subQ6,subQ4,subQ12,subQ10,subQ9,subQ11])],"isStart":false})})})});}
            var sketch = newSketch(context, id + "F21", { "sketchPlane" : qUnion([Q0])});
            skLineSegment(sketch, "E37.bottom", {"start": v(11.45, -0.08) * mm, "end": v(13.55, -0.08) * mm});
            skLineSegment(sketch, "E37.top", {"start": v(11.45, 4.92) * mm, "end": v(13.55, 4.92) * mm});
            skLineSegment(sketch, "E37.left", {"start": v(11.45, -0.08) * mm, "end": v(11.45, 4.92) * mm});
            skLineSegment(sketch, "E37.right", {"start": v(13.55, -0.08) * mm, "end": v(13.55, 4.92) * mm});
            skArc(sketch, "E38", {"start": v(13.55, 4.92) * mm, "mid": v(12.5, 5.97) * mm, "end": v(11.45, 4.92) * mm});
            skSolve(sketch);
        }
        {
            var Q0;
            Q0=makeQuery(id+"F16.imprint","IMPRINT",FACE,{"disambiguationData":[TD([[makeQuery(id+"F16.imprint","IMPRINT",EDGE,{"derivedFrom":sQuery(id+"F16.wireOp",EDGE,"E27.bottom")}),1.0]])]});
            var Q1;
            Q1=makeQuery(id+"F16.imprint","IMPRINT",FACE,{"disambiguationData":[TD([[makeQuery(id+"F16.imprint","IMPRINT",EDGE,{"derivedFrom":sQuery(id+"F16.wireOp",EDGE,"E27.top")}),1.0]])]});
            var Q2;
            Q2=makeQuery(id+"F17.imprint","IMPRINT",FACE,{"disambiguationData":[TD([[makeQuery(id+"F17.imprint","IMPRINT",EDGE,{"derivedFrom":sQuery(id+"F17.wireOp",EDGE,"E29.bottom")}),1.0]])]});
            var Q3;
            Q3=makeQuery(id+"F17.imprint","IMPRINT",FACE,{"disambiguationData":[TD([[makeQuery(id+"F17.imprint","IMPRINT",EDGE,{"derivedFrom":sQuery(id+"F17.wireOp",EDGE,"E29.top")}),1.0]])]});
            var Q4;
            Q4=makeQuery(id+"F18.imprint","IMPRINT",FACE,{"disambiguationData":[TD([[makeQuery(id+"F18.imprint","IMPRINT",EDGE,{"derivedFrom":sQuery(id+"F18.wireOp",EDGE,"E31.top")}),1.0]])]});
            var Q5;
            Q5=makeQuery(id+"F18.imprint","IMPRINT",FACE,{"disambiguationData":[TD([[makeQuery(id+"F18.imprint","IMPRINT",EDGE,{"derivedFrom":sQuery(id+"F18.wireOp",EDGE,"E31.bottom")}),1.0]])]});
            var Q6;
            Q6=makeQuery(id+"F19.imprint","IMPRINT",FACE,{"disambiguationData":[TD([[makeQuery(id+"F19.imprint","IMPRINT",EDGE,{"derivedFrom":sQuery(id+"F19.wireOp",EDGE,"E33.top")}),1.0]])]});
            var Q7;
            Q7=makeQuery(id+"F19.imprint","IMPRINT",FACE,{"disambiguationData":[TD([[makeQuery(id+"F19.imprint","IMPRINT",EDGE,{"derivedFrom":sQuery(id+"F19.wireOp",EDGE,"E33.bottom")}),1.0]])]});
            var Q8;
            Q8=makeQuery(id+"F20.imprint","IMPRINT",FACE,{"disambiguationData":[TD([[makeQuery(id+"F20.imprint","IMPRINT",EDGE,{"derivedFrom":sQuery(id+"F20.wireOp",EDGE,"E35.top")}),1.0]])]});
            var Q9;
            Q9=makeQuery(id+"F20.imprint","IMPRINT",FACE,{"disambiguationData":[TD([[makeQuery(id+"F20.imprint","IMPRINT",EDGE,{"derivedFrom":sQuery(id+"F20.wireOp",EDGE,"E35.bottom")}),1.0]])]});
            var Q10;
            Q10=makeQuery(id+"F21.imprint","IMPRINT",FACE,{"disambiguationData":[TD([[makeQuery(id+"F21.imprint","IMPRINT",EDGE,{"derivedFrom":sQuery(id+"F21.wireOp",EDGE,"E37.top")}),1.0]])]});
            var Q11;
            Q11=makeQuery(id+"F21.imprint","IMPRINT",FACE,{"disambiguationData":[TD([[makeQuery(id+"F21.imprint","IMPRINT",EDGE,{"derivedFrom":sQuery(id+"F21.wireOp",EDGE,"E37.bottom")}),1.0]])]});
            extrude(context, id + "F22", {"entities" : qUnion([Q0, Q1, Q2, Q3, Q4, Q5, Q6, Q7, Q8, Q9, Q10, Q11]), "operationType" : NewBodyOperationType.REMOVE, "endBound" : BoundingType.SYMMETRIC, "oppositeDirection" : true, "depth" : 5 * mm});
        }
        {
            var Q0;
            Q0=makeQuery(id+"F2.opExtrude","SWEPT_EDGE",EDGE,{"disambiguationData":[OSD([sQuery(id+"F0.wireOp",EDGE,"E0.top"),sQuery(id+"F0.wireOp",EDGE,"E0.left")])]});
            var Q1;
            Q1=makeQuery(id+"F2.opExtrude","SWEPT_EDGE",EDGE,{"disambiguationData":[OSD([sQuery(id+"F0.wireOp",EDGE,"E0.top"),sQuery(id+"F0.wireOp",EDGE,"E0.right")])]});
            var Q2;
            Q2=makeQuery(id+"F2.opExtrude","SWEPT_EDGE",EDGE,{"disambiguationData":[OSD([sQuery(id+"F0.wireOp",EDGE,"E0.bottom"),sQuery(id+"F0.wireOp",EDGE,"E0.right")])]});
            var Q3;
            Q3=makeQuery(id+"F2.opExtrude","SWEPT_EDGE",EDGE,{"disambiguationData":[OSD([sQuery(id+"F0.wireOp",EDGE,"E0.bottom"),sQuery(id+"F0.wireOp",EDGE,"E0.left")])]});
            var Q4;
            Q4=makeQuery(id+"F4.opExtrude","CAP_EDGE",EDGE,{"disambiguationData":[OSD([sQuery(id+"F3.wireOp",EDGE,"E2.left")])],"isStart":false});
            var Q5;
            Q5=makeQuery(id+"F4.opExtrude","CAP_EDGE",EDGE,{"disambiguationData":[OSD([sQuery(id+"F3.wireOp",EDGE,"E2.right")])],"isStart":false});
            var Q6;
            Q6=makeQuery(id+"F6.opExtrude","CAP_EDGE",EDGE,{"disambiguationData":[OSD([sQuery(id+"F5.wireOp",EDGE,"E3.right")])],"isStart":false});
            var Q7;
            Q7=makeQuery(id+"F6.opExtrude","CAP_EDGE",EDGE,{"disambiguationData":[OSD([sQuery(id+"F5.wireOp",EDGE,"E3.left")])],"isStart":false});
            fillet(context, id + "F23", {"entities" : qUnion([Q0, Q1, Q2, Q3, Q4, Q5, Q6, Q7]), "radius" : 1 * mm, "tangentPropagation" : true, "allowEdgeOverflow" : false});
        }
        {
            var Q0;
            Q0=makeQuery(id+"F15.opExtrude","CAP_EDGE",EDGE,{"disambiguationData":[OSD([sQuery(id+"F14.wireOp",EDGE,"E20.left")])],"isStart":false});
            var Q1;
            Q1=makeQuery(id+"F15.opExtrude","CAP_EDGE",EDGE,{"disambiguationData":[OSD([sQuery(id+"F14.wireOp",EDGE,"E20.right")])],"isStart":false});
            var Q2;
            Q2=makeQuery(id+"F15.opExtrude","CAP_EDGE",EDGE,{"disambiguationData":[OSD([sQuery(id+"F14.wireOp",EDGE,"E21.left")])],"isStart":false});
            var Q3;
            Q3=makeQuery(id+"F15.opExtrude","CAP_EDGE",EDGE,{"disambiguationData":[OSD([sQuery(id+"F14.wireOp",EDGE,"E21.right")])],"isStart":false});
            var Q4;
            Q4=makeQuery(id+"F15.opExtrude","CAP_EDGE",EDGE,{"disambiguationData":[OSD([sQuery(id+"F14.wireOp",EDGE,"E22.left")])],"isStart":false});
            var Q5;
            Q5=makeQuery(id+"F15.opExtrude","CAP_EDGE",EDGE,{"disambiguationData":[OSD([sQuery(id+"F14.wireOp",EDGE,"E22.right")])],"isStart":false});
            var Q6;
            Q6=makeQuery(id+"F15.opExtrude","CAP_EDGE",EDGE,{"disambiguationData":[OSD([sQuery(id+"F14.wireOp",EDGE,"E23.left")])],"isStart":false});
            var Q7;
            Q7=makeQuery(id+"F15.opExtrude","CAP_EDGE",EDGE,{"disambiguationData":[OSD([sQuery(id+"F14.wireOp",EDGE,"E23.right")])],"isStart":false});
            var Q8;
            Q8=makeQuery(id+"F15.opExtrude","CAP_EDGE",EDGE,{"disambiguationData":[OSD([sQuery(id+"F14.wireOp",EDGE,"E24.left")])],"isStart":false});
            var Q9;
            Q9=makeQuery(id+"F15.opExtrude","CAP_EDGE",EDGE,{"disambiguationData":[OSD([sQuery(id+"F14.wireOp",EDGE,"E24.right")])],"isStart":false});
            var Q10;
            Q10=makeQuery(id+"F15.opExtrude","CAP_EDGE",EDGE,{"disambiguationData":[OSD([sQuery(id+"F14.wireOp",EDGE,"E25.left")])],"isStart":false});
            var Q11;
            Q11=makeQuery(id+"F15.opExtrude","CAP_EDGE",EDGE,{"disambiguationData":[OSD([sQuery(id+"F14.wireOp",EDGE,"E25.right")])],"isStart":false});
            var Q12;
            Q12=makeQuery(id+"F15.opExtrude","CAP_EDGE",EDGE,{"disambiguationData":[OSD([sQuery(id+"F14.wireOp",EDGE,"E26.left")])],"isStart":false});
            var Q13;
            Q13=makeQuery(id+"F15.opExtrude","CAP_EDGE",EDGE,{"disambiguationData":[OSD([sQuery(id+"F14.wireOp",EDGE,"E26.right")])],"isStart":false});
            fillet(context, id + "F24", {"entities" : qUnion([Q0, Q1, Q2, Q3, Q4, Q5, Q6, Q7, Q8, Q9, Q10, Q11, Q12, Q13]), "radius" : 1.1 * mm, "tangentPropagation" : true, "allowEdgeOverflow" : false});
        }
        {
            var Q0;
            Q0=makeQuery(id+"F2.opExtrude","SWEPT_BODY",BODY,{"disambiguationData":[OSD([sQuery(id+"F0.wireOp",EDGE,"E0.bottom"),sQuery(id+"F0.wireOp",EDGE,"E0.top"),sQuery(id+"F0.wireOp",EDGE,"E0.left"),sQuery(id+"F0.wireOp",EDGE,"E0.right"),sQuery(id+"F1.wireOp",EDGE,"E1.bottom"),sQuery(id+"F1.wireOp",EDGE,"E1.top"),sQuery(id+"F1.wireOp",EDGE,"E1.left"),sQuery(id+"F1.wireOp",EDGE,"E1.right")])]});
            var Q1;
            Q1=makeQuery(id+"F0.imprint","IMPRINT",FACE,{"disambiguationData":[TD([[makeQuery(id+"F0.imprint","IMPRINT",EDGE,{"derivedFrom":sQuery(id+"F0.wireOp",EDGE,"E0.bottom")}),1.0]])]});
            mirror(context, id + "F25", {"operationType" : NewBodyOperationType.ADD, "entities" : qUnion([Q0]), "mirrorPlane" : qUnion([Q1])});
        }
        {
            var Q0;
            Q0=makeQuery(id+"F0.imprint","IMPRINT",FACE,{"disambiguationData":[TD([[makeQuery(id+"F0.imprint","IMPRINT",EDGE,{"derivedFrom":sQuery(id+"F0.wireOp",EDGE,"E0.bottom")}),1.0]])]});
            var sketch = newSketch(context, id + "F26", { "sketchPlane" : qUnion([Q0])});
            skLineSegment(sketch, "E39.bottom", {"start": v(-9.8, 34.62) * mm, "end": v(9.8, 34.62) * mm});
            skLineSegment(sketch, "E39.top", {"start": v(-9.8, 10.92) * mm, "end": v(9.8, 10.92) * mm});
            skLineSegment(sketch, "E39.left", {"start": v(-9.8, 34.62) * mm, "end": v(-9.8, 10.92) * mm});
            skLineSegment(sketch, "E39.right", {"start": v(9.8, 34.62) * mm, "end": v(9.8, 10.92) * mm});
            skSolve(sketch);
        }
        {
            var Q0;
            Q0=makeQuery(id+"F26.imprint","IMPRINT",FACE,{"disambiguationData":[TD([[makeQuery(id+"F26.imprint","IMPRINT",EDGE,{"derivedFrom":sQuery(id+"F26.wireOp",EDGE,"E39.bottom")}),-1.0]])]});
            var sketch = newSketch(context, id + "F27", { "sketchPlane" : qUnion([Q0])});
            skLineSegment(sketch, "E40.bottom", {"start": v(-8.8, 33.62) * mm, "end": v(8.8, 33.62) * mm});
            skLineSegment(sketch, "E40.top", {"start": v(-8.8, 11.92) * mm, "end": v(8.8, 11.92) * mm});
            skLineSegment(sketch, "E40.left", {"start": v(-8.8, 33.62) * mm, "end": v(-8.8, 11.92) * mm});
            skLineSegment(sketch, "E40.right", {"start": v(8.8, 33.62) * mm, "end": v(8.8, 11.92) * mm});
            skSolve(sketch);
        }
        {
            var Q0;
            Q0=makeQuery(id+"F27.imprint","IMPRINT",FACE,{"disambiguationData":[TD([[makeQuery(id+"F27.imprint","IMPRINT",EDGE,{"derivedFrom":sQuery(id+"F27.wireOp",EDGE,"E40.bottom")}),1.0]])]});
            extrude(context, id + "F28", {"entities" : qUnion([Q0]), "operationType" : NewBodyOperationType.ADD, "endBound" : BoundingType.SYMMETRIC, "depth" : 35 * mm});
        }
        {
            var Q0;
            Q0=makeQuery(id+"F3.imprint","IMPRINT",FACE,{"disambiguationData":[TD([[makeQuery(id+"F3.imprint","IMPRINT",EDGE,{"derivedFrom":makeQuery(id+"F2.opExtrude","CAP_EDGE",EDGE,{"disambiguationData":[OSD([sQuery(id+"F1.wireOp",EDGE,"E1.bottom")])],"isStart":false})}),-1.0]])]});
            var sketch = newSketch(context, id + "F29", { "sketchPlane" : qUnion([Q0])});
            skLineSegment(sketch, "E41.bottom", {"start": v(-18.55, -0.13) * mm, "end": v(18.5, -0.13) * mm});
            skLineSegment(sketch, "E41.top", {"start": v(-18.55, 1.12) * mm, "end": v(18.5, 1.12) * mm});
            skLineSegment(sketch, "E41.left", {"start": v(-18.55, -0.13) * mm, "end": v(-18.55, 1.12) * mm});
            skLineSegment(sketch, "E41.right", {"start": v(18.5, -0.13) * mm, "end": v(18.5, 1.12) * mm});
            skSolve(sketch);
        }
        {
            var Q0;
            Q0=qSketchRegion(id+"F29",true);
            extrude(context, id + "F30", {"entities" : qUnion([Q0]), "operationType" : NewBodyOperationType.REMOVE, "depth" : 2 * mm});
        }
    });
